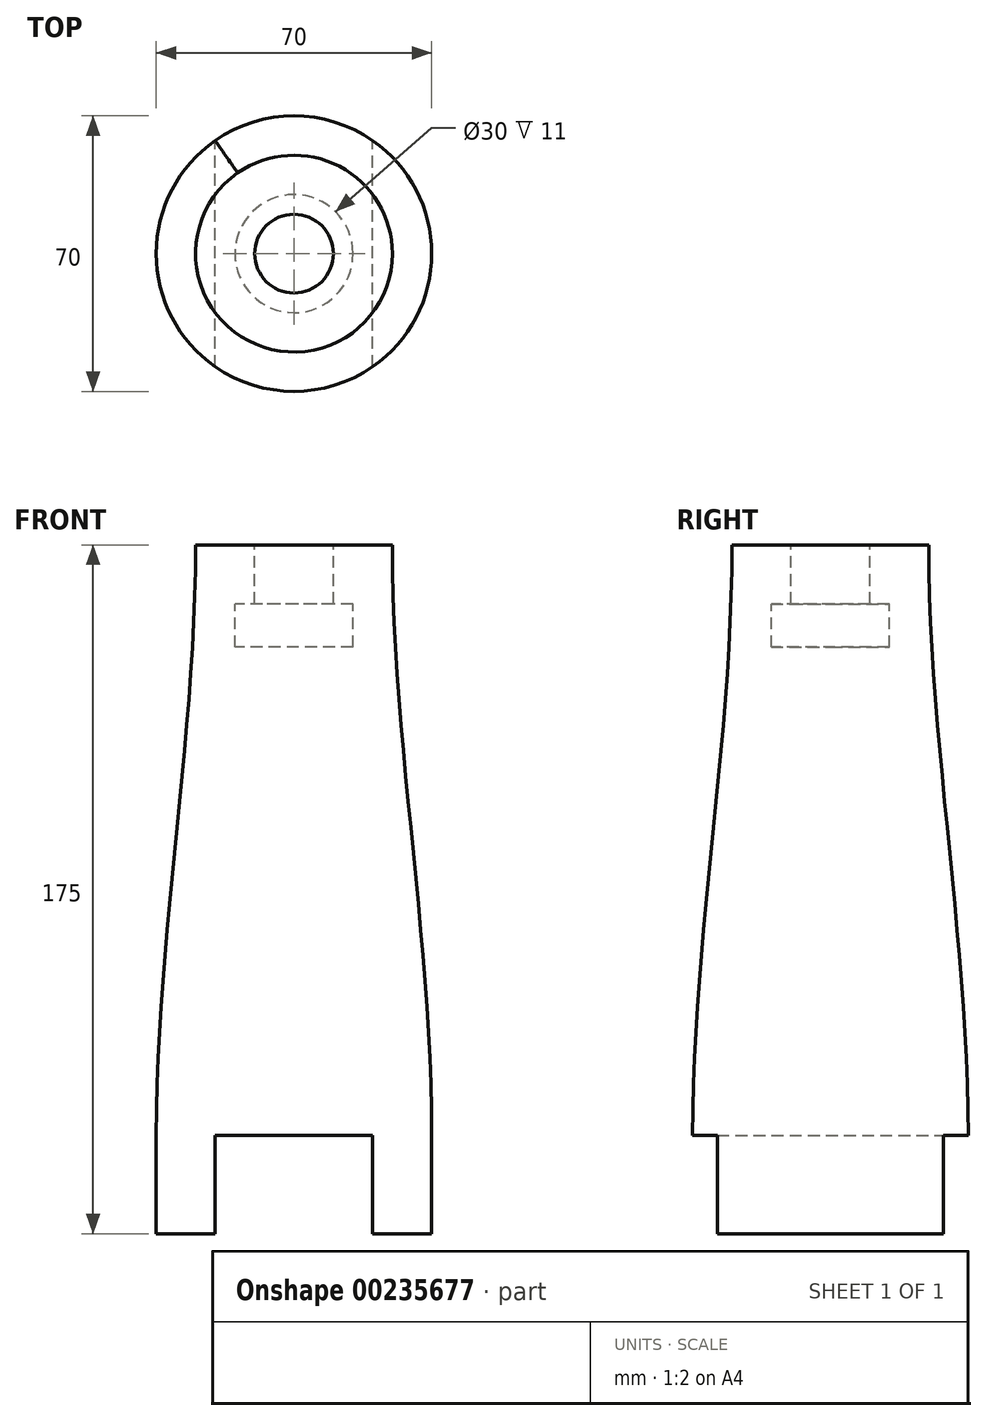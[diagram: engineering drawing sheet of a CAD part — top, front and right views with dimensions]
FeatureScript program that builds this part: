
annotation { "Feature Type Name" : "Feature", "Feature Type Description" : "" }
export const myFeature = defineFeature(function(context is Context, id is Id, definition is map)
    precondition{}
    {
        {
            var Q0;
            Q0=qCreatedBy(makeId("Top.planeOp"),FACE);
            var sketch = newSketch(context, id + "F0", { "sketchPlane" : qUnion([Q0])});
            skCircle(sketch, "E0", {"center": v(0, 0) * mm, "radius": 25 * mm});
            skSolve(sketch);
        }
        {
            var Q0;
            Q0=qCreatedBy(makeId("Top.planeOp"),FACE);
            cPlane(context, id + "F1", {"entities" : qUnion([Q0]), "cplaneType" : CPlaneType.OFFSET, "offset" : 150 * mm, "oppositeDirection" : true, "width" : 150 * mm, "height" : 150 * mm});
        }
        {
            var Q0;
            Q0=qCreatedBy(id+"F1.planeOp",FACE);
            var sketch = newSketch(context, id + "F2", { "sketchPlane" : qUnion([Q0])});
            skCircle(sketch, "E1", {"center": v(0, 0) * mm, "radius": 35 * mm});
            skSolve(sketch);
        }
        {
            var Q0;
            Q0=makeQuery(id+"F0.imprint","IMPRINT",FACE,{"disambiguationData":[TD([[makeQuery(id+"F0.imprint","IMPRINT",EDGE,{"derivedFrom":sQuery(id+"F0.wireOp",EDGE,"E0")}),1.0]])]});
            var Q1;
            Q1=makeQuery(id+"F2.imprint","IMPRINT",FACE,{"disambiguationData":[TD([[makeQuery(id+"F2.imprint","IMPRINT",EDGE,{"derivedFrom":sQuery(id+"F2.wireOp",EDGE,"E1")}),1.0]])]});
            loft(context, id + "F3", {"startCondition" : LoftEndDerivativeType.NORMAL_TO_PROFILE, "startMagnitude" : 1, "endCondition" : LoftEndDerivativeType.NORMAL_TO_PROFILE, "endMagnitude" : 1, "sheetProfilesArray" : [{ "sheetProfileEntities" : qUnion([Q0]) }, { "sheetProfileEntities" : qUnion([Q1]) }]});
        }
        {
            var Q0;
            Q0=makeQuery(id+"F2.imprint","IMPRINT",FACE,{"disambiguationData":[TD([[makeQuery(id+"F2.imprint","IMPRINT",EDGE,{"derivedFrom":sQuery(id+"F2.wireOp",EDGE,"E1")}),1.0]])]});
            var sketch = newSketch(context, id + "F4", { "sketchPlane" : qUnion([Q0])});
            skArc(sketch, "E2.0", {"start": v(20, -28.72) * mm, "mid": v(35, 0) * mm, "end": v(20, 28.72) * mm});
            skLineSegment(sketch, "E3", {"start": v(-20, -28.72) * mm, "end": v(-20, 28.72) * mm});
            skLineSegment(sketch, "E4", {"start": v(20, -28.72) * mm, "end": v(20, 28.72) * mm});
            skArc(sketch, "E5.trimOffspring", {"start": v(-20, 28.72) * mm, "mid": v(-35, 0) * mm, "end": v(-20, -28.72) * mm});
            skSolve(sketch);
        }
        {
            var Q0;
            Q0 = qSketchRegion(id + "F4", true);
            extrude(context, id + "F5", {"entities" : qUnion([Q0]), "operationType" : NewBodyOperationType.ADD, "oppositeDirection" : true, "depth" : 25 * mm});
        }
        {
            var Q0;
            Q0=qCreatedBy(makeId("Front.planeOp"),FACE);
            var sketch = newSketch(context, id + "F6", { "sketchPlane" : qUnion([Q0])});
            skLineSegment(sketch, "E6", {"start": v(-10, 0) * mm, "end": v(-10, -15) * mm});
            skLineSegment(sketch, "E7", {"start": v(-10, -15) * mm, "end": v(-15, -15) * mm});
            skLineSegment(sketch, "E8", {"start": v(-15, -15) * mm, "end": v(-15, -26) * mm});
            skLineSegment(sketch, "E9", {"start": v(-15, -26) * mm, "end": v(0, -26) * mm});
            skLineSegment(sketch, "E10", {"start": v(0, -26) * mm, "end": v(0, 0) * mm});
            skLineSegment(sketch, "E11", {"start": v(-10, 0) * mm, "end": v(0, 0) * mm});
            skSolve(sketch);
        }
        {
            var Q0;
            Q0 = qSketchRegion(id + "F6", true);
            var Q1;
            Q1=sQuery(id+"F6.wireOp",EDGE,"E10");
            revolve(context, id + "F7", {"operationType" : NewBodyOperationType.REMOVE, "entities" : qUnion([Q0]), "axis" : qUnion([Q1]), "revolveType" : RevolveType.FULL, "oppositeDirection" : true});
        }
    });
